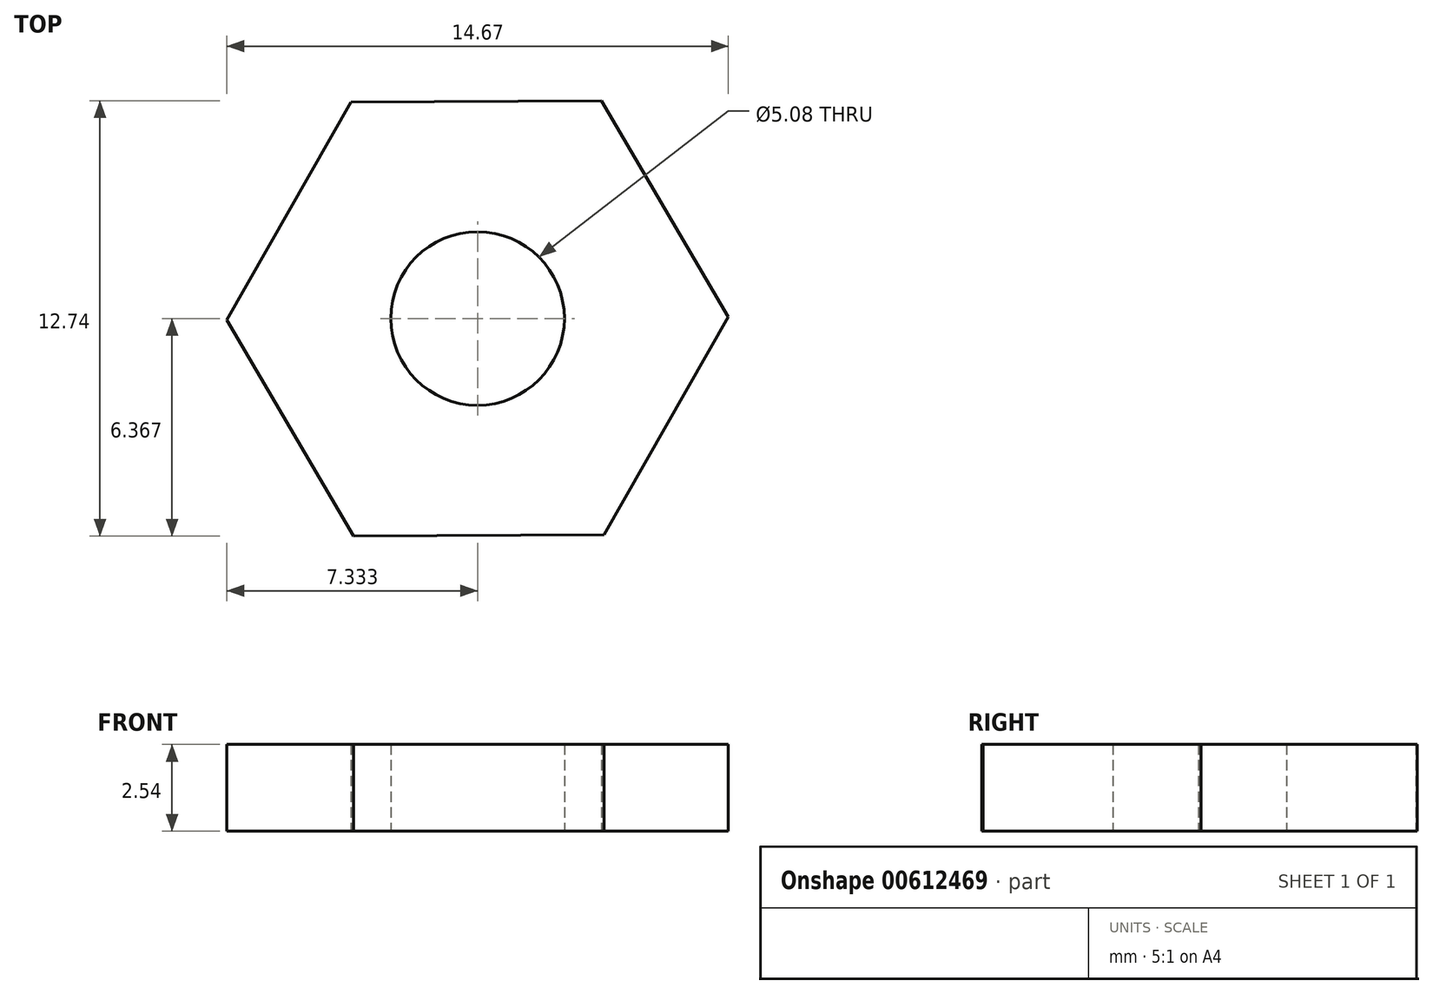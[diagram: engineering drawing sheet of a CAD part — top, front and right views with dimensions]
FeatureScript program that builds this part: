
annotation { "Feature Type Name" : "Feature", "Feature Type Description" : "" }
export const myFeature = defineFeature(function(context is Context, id is Id, definition is map)
    precondition{}
    {
        {
            var Q0;
            Q0=qCreatedBy(makeId("Top.planeOp"),FACE);
            var sketch = newSketch(context, id + "F0", { "sketchPlane" : qUnion([Q0])});
            skCircle(sketch, "E0.cCircle", {"center": v(-6.98, -6.1) * mm, "radius": 6.35 * mm, "construction": true});
            skLineSegment(sketch, "E0.0", {"start": v(-3.35, 0.28) * mm, "end": v(0.36, -6.05) * mm});
            skLineSegment(sketch, "E0.1", {"start": v(0.36, -6.05) * mm, "end": v(-3.27, -12.42) * mm});
            skLineSegment(sketch, "E0.2", {"start": v(-3.27, -12.42) * mm, "end": v(-10.6, -12.46) * mm});
            skLineSegment(sketch, "E0.3", {"start": v(-10.6, -12.46) * mm, "end": v(-14.3, -6.13) * mm});
            skLineSegment(sketch, "E0.4", {"start": v(-14.3, -6.13) * mm, "end": v(-10.68, 0.24) * mm});
            skLineSegment(sketch, "E0.5", {"start": v(-10.68, 0.24) * mm, "end": v(-3.35, 0.28) * mm});
            skPoint(sketch, "E0.0.midPoint", {"position": v(-1.5, -2.89) * mm});
            skCircle(sketch, "E1", {"center": v(-6.98, -6.1) * mm, "radius": 2.54 * mm});
            skSolve(sketch);
        }
        {
            var Q0;
            Q0 = qSketchRegion(id + "F0", true);
            extrude(context, id + "F1", {"entities" : qUnion([Q0]), "depth" : 2.54 * mm, "offsetDistance" : 25.4 * mm});
        }
    });
